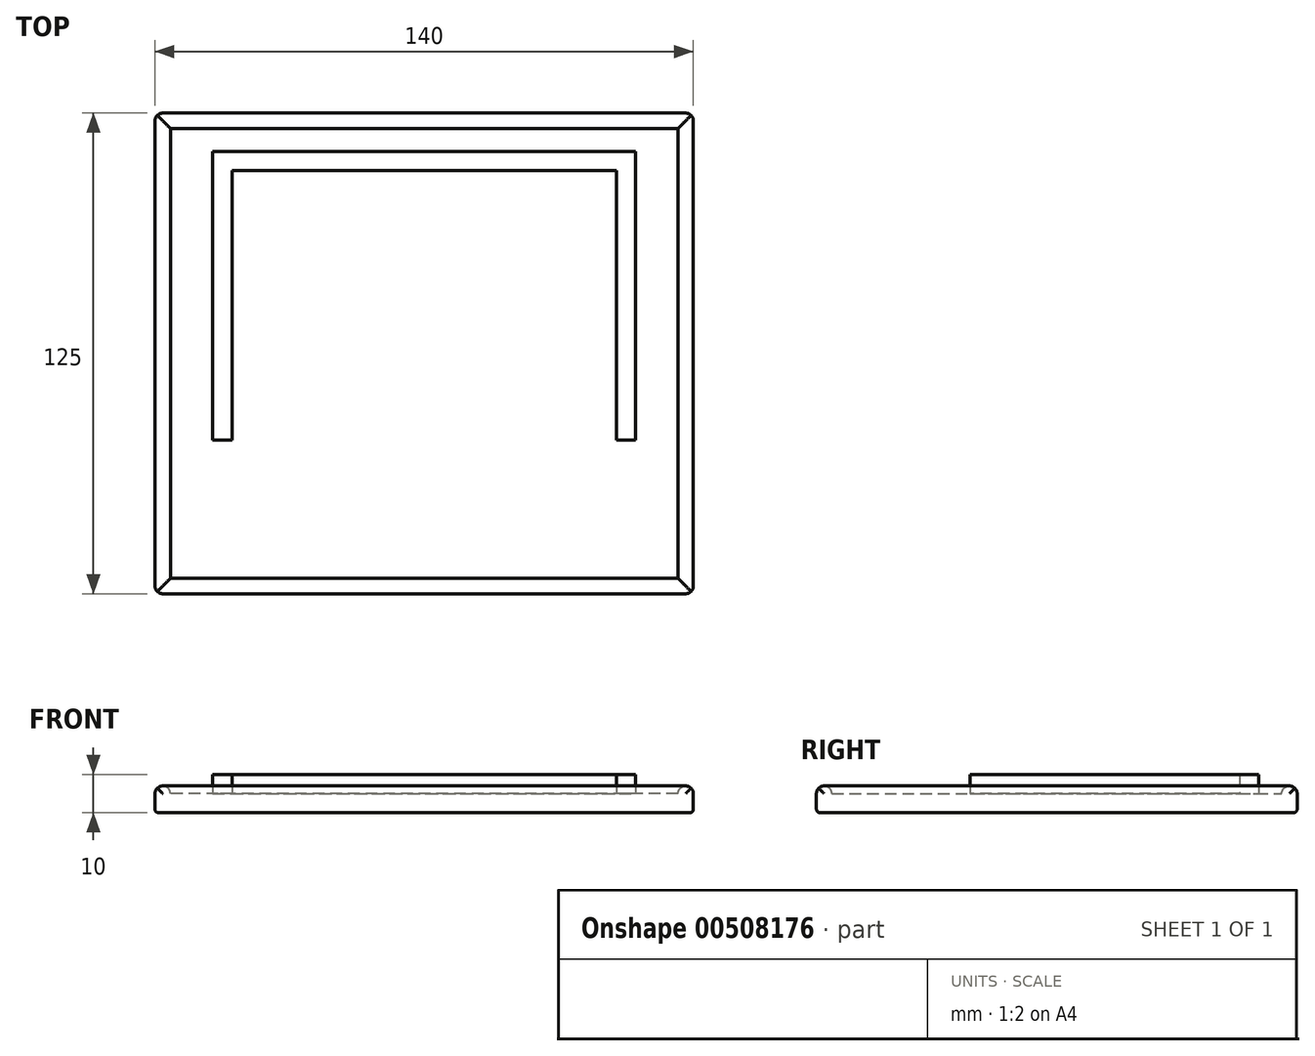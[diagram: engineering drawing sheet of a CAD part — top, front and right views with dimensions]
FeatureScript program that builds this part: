
annotation { "Feature Type Name" : "Feature", "Feature Type Description" : "" }
export const myFeature = defineFeature(function(context is Context, id is Id, definition is map)
    precondition{}
    {
        {
            var Q0;
            Q0=qCreatedBy(makeId("Top.planeOp"),FACE);
            var sketch = newSketch(context, id + "F0", { "sketchPlane" : qUnion([Q0])});
            skLineSegment(sketch, "E0.bottom", {"start": v(70, 62.5) * mm, "end": v(-70, 62.5) * mm});
            skLineSegment(sketch, "E0.top", {"start": v(70, -62.5) * mm, "end": v(-70, -62.5) * mm});
            skLineSegment(sketch, "E0.left", {"start": v(70, 62.5) * mm, "end": v(70, -62.5) * mm});
            skLineSegment(sketch, "E0.right", {"start": v(-70, 62.5) * mm, "end": v(-70, -62.5) * mm});
            skPoint(sketch, "E0.middle", {"position": v(0, 0) * mm});
            skSolve(sketch);
        }
        {
            var Q0;
            Q0=makeQuery(id+"F0.imprint","IMPRINT",FACE,{"disambiguationData":[TD([[makeQuery(id+"F0.imprint","IMPRINT",EDGE,{"derivedFrom":sQuery(id+"F0.wireOp",EDGE,"E0.bottom")}),1.0]])]});
            extrude(context, id + "F1", {"entities" : qUnion([Q0]), "depth" : 5 * mm, "offsetDistance" : 25 * mm});
        }
        {
            var Q0;
            Q0=makeQuery(id+"F1.opExtrude","CAP_FACE",FACE,{"disambiguationData":[OSD([sQuery(id+"F0.wireOp",EDGE,"E0.bottom"),sQuery(id+"F0.wireOp",EDGE,"E0.top"),sQuery(id+"F0.wireOp",EDGE,"E0.left"),sQuery(id+"F0.wireOp",EDGE,"E0.right")])],"isStart":false});
            var sketch = newSketch(context, id + "F2", { "sketchPlane" : qUnion([Q0])});
            skLineSegment(sketch, "E1", {"start": v(23.4, -62.5) * mm, "end": v(23.4, -22.5) * mm});
            skLineSegment(sketch, "E2", {"start": v(55, -22.5) * mm, "end": v(-55, -22.5) * mm});
            skLineSegment(sketch, "E3", {"start": v(-55, -22.5) * mm, "end": v(-55, 52.5) * mm});
            skLineSegment(sketch, "E4", {"start": v(-55, 52.5) * mm, "end": v(55, 52.5) * mm});
            skLineSegment(sketch, "E5", {"start": v(55, 52.5) * mm, "end": v(55, -22.5) * mm});
            skLineSegment(sketch, "E6", {"start": v(-50, 47.5) * mm, "end": v(50, 47.5) * mm});
            skLineSegment(sketch, "E7", {"start": v(50, 47.5) * mm, "end": v(50, -17.5) * mm});
            skLineSegment(sketch, "E8", {"start": v(-50, 47.5) * mm, "end": v(-50, -17.5) * mm});
            skLineSegment(sketch, "E9", {"start": v(-50, -17.5) * mm, "end": v(50, -17.5) * mm});
            skLineSegment(sketch, "E10", {"start": v(-66, 58.5) * mm, "end": v(66, 58.5) * mm});
            skLineSegment(sketch, "E11", {"start": v(66, 58.5) * mm, "end": v(66, -58.5) * mm});
            skLineSegment(sketch, "E12", {"start": v(66, -58.5) * mm, "end": v(-66, -58.5) * mm});
            skLineSegment(sketch, "E13", {"start": v(-66, -58.5) * mm, "end": v(-66, 58.5) * mm});
            skLineSegment(sketch, "E14", {"start": v(-50, -17.5) * mm, "end": v(-50, -22.5) * mm});
            skLineSegment(sketch, "E15", {"start": v(50, -17.5) * mm, "end": v(50, -22.5) * mm});
            skSolve(sketch);
        }
        {
            var Q0;
            {var subQ0=sQuery(id+"F2.wireOp",EDGE,"E3");Q0=makeQuery(id+"F2.imprint","IMPRINT",FACE,{"disambiguationData":[TD([[makeQuery(id+"F2.imprint","IMPRINT",EDGE,{"derivedFrom":subQ0}),-1.0]])]});}
            extrude(context, id + "F3", {"entities" : qUnion([Q0]), "operationType" : NewBodyOperationType.ADD, "depth" : 5 * mm, "offsetDistance" : 25 * mm});
        }
        {
            var Q0;
            Q0=makeQuery(id+"F2.imprint","IMPRINT",FACE,{"disambiguationData":[TD([[makeQuery(id+"F2.imprint","IMPRINT",EDGE,{"derivedFrom":sQuery(id+"F2.wireOp",EDGE,"E10")}),1.0]])]});
            extrude(context, id + "F4", {"entities" : qUnion([Q0]), "operationType" : NewBodyOperationType.ADD, "depth" : 2 * mm, "offsetDistance" : 25 * mm});
        }
        {
            var Q0;
            Q0=makeQuery(id+"F4.opExtrude","CAP_EDGE",EDGE,{"disambiguationData":[OSD([sQuery(id+"F2.wireOp",EDGE,"E13")])],"isStart":false});
            var Q1;
            Q1=makeQuery(id+"F4.opExtrude","CAP_EDGE",EDGE,{"disambiguationData":[OSD([sQuery(id+"F0.wireOp",EDGE,"E0.right")])],"isStart":false});
            var Q2;
            Q2=makeQuery(id+"F4.opExtrude","CAP_EDGE",EDGE,{"disambiguationData":[OSD([sQuery(id+"F2.wireOp",EDGE,"E10")])],"isStart":false});
            var Q3;
            Q3=makeQuery(id+"F4.opExtrude","CAP_EDGE",EDGE,{"disambiguationData":[OSD([sQuery(id+"F0.wireOp",EDGE,"E0.bottom")])],"isStart":false});
            var Q4;
            Q4=makeQuery(id+"F4.opExtrude","CAP_EDGE",EDGE,{"disambiguationData":[OSD([sQuery(id+"F2.wireOp",EDGE,"E12")])],"isStart":false});
            var Q5;
            Q5=makeQuery(id+"F4.opExtrude","CAP_EDGE",EDGE,{"disambiguationData":[OSD([sQuery(id+"F0.wireOp",EDGE,"E0.top")])],"isStart":false});
            var Q6;
            Q6=makeQuery(id+"F4.opExtrude","CAP_EDGE",EDGE,{"disambiguationData":[OSD([sQuery(id+"F2.wireOp",EDGE,"E11")])],"isStart":false});
            var Q7;
            Q7=makeQuery(id+"F4.opExtrude","CAP_EDGE",EDGE,{"disambiguationData":[OSD([sQuery(id+"F0.wireOp",EDGE,"E0.left")])],"isStart":false});
            fillet(context, id + "F5", {"entities" : qUnion([Q0, Q1, Q2, Q3, Q4, Q5, Q6, Q7]), "radius" : 2 * mm, "tangentPropagation" : true, "allowEdgeOverflow" : false});
        }
        {
            var Q0;
            {var subQ0=sQuery(id+"F0.wireOp",EDGE,"E0.right");var subQ1=sQuery(id+"F0.wireOp",EDGE,"E0.bottom");Q0=makeQuery(id+"F4.boolean.opBoolean","MERGE",EDGE,{"derivedFrom":[makeQuery(id+"F1.opExtrude","SWEPT_EDGE",EDGE,{"disambiguationData":[OSD([subQ1,subQ0])]}),makeQuery(id+"F4.opExtrude","SWEPT_EDGE",EDGE,{"disambiguationData":[OSD([subQ1,subQ0])]})]});}
            var Q1;
            {var subQ0=sQuery(id+"F0.wireOp",EDGE,"E0.right");var subQ1=sQuery(id+"F0.wireOp",EDGE,"E0.top");Q1=makeQuery(id+"F4.boolean.opBoolean","MERGE",EDGE,{"derivedFrom":[makeQuery(id+"F1.opExtrude","SWEPT_EDGE",EDGE,{"disambiguationData":[OSD([subQ1,subQ0])]}),makeQuery(id+"F4.opExtrude","SWEPT_EDGE",EDGE,{"disambiguationData":[OSD([subQ1,subQ0])]})]});}
            var Q2;
            {var subQ0=sQuery(id+"F0.wireOp",EDGE,"E0.left");var subQ1=sQuery(id+"F0.wireOp",EDGE,"E0.top");Q2=makeQuery(id+"F4.boolean.opBoolean","MERGE",EDGE,{"derivedFrom":[makeQuery(id+"F1.opExtrude","SWEPT_EDGE",EDGE,{"disambiguationData":[OSD([subQ1,subQ0])]}),makeQuery(id+"F4.opExtrude","SWEPT_EDGE",EDGE,{"disambiguationData":[OSD([subQ1,subQ0])]})]});}
            var Q3;
            {var subQ0=sQuery(id+"F0.wireOp",EDGE,"E0.left");var subQ1=sQuery(id+"F0.wireOp",EDGE,"E0.bottom");Q3=makeQuery(id+"F4.boolean.opBoolean","MERGE",EDGE,{"derivedFrom":[makeQuery(id+"F1.opExtrude","SWEPT_EDGE",EDGE,{"disambiguationData":[OSD([subQ1,subQ0])]}),makeQuery(id+"F4.opExtrude","SWEPT_EDGE",EDGE,{"disambiguationData":[OSD([subQ1,subQ0])]})]});}
            fillet(context, id + "F6", {"entities" : qUnion([Q0, Q1, Q2, Q3]), "radius" : 2 * mm, "tangentPropagation" : true, "allowEdgeOverflow" : false});
        }
        {
            var Q0;
            Q0=makeQuery(id+"F1.opExtrude","CAP_EDGE",EDGE,{"disambiguationData":[OSD([sQuery(id+"F0.wireOp",EDGE,"E0.top")])],"isStart":true});
            var Q1;
            Q1=makeQuery(id+"F1.opExtrude","CAP_EDGE",EDGE,{"disambiguationData":[OSD([sQuery(id+"F0.wireOp",EDGE,"E0.right")])],"isStart":true});
            var Q2;
            {var subQ0=sQuery(id+"F0.wireOp",EDGE,"E0.right");var subQ1=sQuery(id+"F0.wireOp",EDGE,"E0.top");Q2=makeQuery(id+"F6.opFillet","BLEND_EDGE",EDGE,{"blendedFrom":[makeQuery(id+"F4.boolean.opBoolean","MERGE",EDGE,{"derivedFrom":[makeQuery(id+"F1.opExtrude","SWEPT_EDGE",EDGE,{"disambiguationData":[OSD([subQ1,subQ0])]}),makeQuery(id+"F4.opExtrude","SWEPT_EDGE",EDGE,{"disambiguationData":[OSD([subQ1,subQ0])]})]}),makeQuery(id+"F1.opExtrude","CAP_FACE",FACE,{"disambiguationData":[OSD([sQuery(id+"F0.wireOp",EDGE,"E0.bottom"),subQ1,sQuery(id+"F0.wireOp",EDGE,"E0.left"),subQ0])],"isStart":true})],"blendedInto":[makeQuery(id+"F1.opExtrude","CAP_FACE",FACE,{"disambiguationData":[OSD([sQuery(id+"F0.wireOp",EDGE,"E0.bottom"),subQ1,sQuery(id+"F0.wireOp",EDGE,"E0.left"),subQ0])],"isStart":true})]});}
            var Q3;
            {var subQ0=sQuery(id+"F0.wireOp",EDGE,"E0.right");var subQ1=sQuery(id+"F0.wireOp",EDGE,"E0.bottom");Q3=makeQuery(id+"F6.opFillet","BLEND_EDGE",EDGE,{"blendedFrom":[makeQuery(id+"F4.boolean.opBoolean","MERGE",EDGE,{"derivedFrom":[makeQuery(id+"F1.opExtrude","SWEPT_EDGE",EDGE,{"disambiguationData":[OSD([subQ1,subQ0])]}),makeQuery(id+"F4.opExtrude","SWEPT_EDGE",EDGE,{"disambiguationData":[OSD([subQ1,subQ0])]})]}),makeQuery(id+"F1.opExtrude","CAP_FACE",FACE,{"disambiguationData":[OSD([subQ1,sQuery(id+"F0.wireOp",EDGE,"E0.top"),sQuery(id+"F0.wireOp",EDGE,"E0.left"),subQ0])],"isStart":true})],"blendedInto":[makeQuery(id+"F1.opExtrude","CAP_FACE",FACE,{"disambiguationData":[OSD([subQ1,sQuery(id+"F0.wireOp",EDGE,"E0.top"),sQuery(id+"F0.wireOp",EDGE,"E0.left"),subQ0])],"isStart":true})]});}
            var Q4;
            Q4=makeQuery(id+"F1.opExtrude","CAP_EDGE",EDGE,{"disambiguationData":[OSD([sQuery(id+"F0.wireOp",EDGE,"E0.bottom")])],"isStart":true});
            var Q5;
            {var subQ0=sQuery(id+"F0.wireOp",EDGE,"E0.left");var subQ1=sQuery(id+"F0.wireOp",EDGE,"E0.top");Q5=makeQuery(id+"F6.opFillet","BLEND_EDGE",EDGE,{"blendedFrom":[makeQuery(id+"F4.boolean.opBoolean","MERGE",EDGE,{"derivedFrom":[makeQuery(id+"F1.opExtrude","SWEPT_EDGE",EDGE,{"disambiguationData":[OSD([subQ1,subQ0])]}),makeQuery(id+"F4.opExtrude","SWEPT_EDGE",EDGE,{"disambiguationData":[OSD([subQ1,subQ0])]})]}),makeQuery(id+"F1.opExtrude","CAP_FACE",FACE,{"disambiguationData":[OSD([sQuery(id+"F0.wireOp",EDGE,"E0.bottom"),subQ1,subQ0,sQuery(id+"F0.wireOp",EDGE,"E0.right")])],"isStart":true})],"blendedInto":[makeQuery(id+"F1.opExtrude","CAP_FACE",FACE,{"disambiguationData":[OSD([sQuery(id+"F0.wireOp",EDGE,"E0.bottom"),subQ1,subQ0,sQuery(id+"F0.wireOp",EDGE,"E0.right")])],"isStart":true})]});}
            var Q6;
            Q6=makeQuery(id+"F1.opExtrude","CAP_EDGE",EDGE,{"disambiguationData":[OSD([sQuery(id+"F0.wireOp",EDGE,"E0.left")])],"isStart":true});
            var Q7;
            {var subQ0=sQuery(id+"F0.wireOp",EDGE,"E0.left");var subQ1=sQuery(id+"F0.wireOp",EDGE,"E0.bottom");Q7=makeQuery(id+"F6.opFillet","BLEND_EDGE",EDGE,{"blendedFrom":[makeQuery(id+"F4.boolean.opBoolean","MERGE",EDGE,{"derivedFrom":[makeQuery(id+"F1.opExtrude","SWEPT_EDGE",EDGE,{"disambiguationData":[OSD([subQ1,subQ0])]}),makeQuery(id+"F4.opExtrude","SWEPT_EDGE",EDGE,{"disambiguationData":[OSD([subQ1,subQ0])]})]}),makeQuery(id+"F1.opExtrude","CAP_FACE",FACE,{"disambiguationData":[OSD([subQ1,sQuery(id+"F0.wireOp",EDGE,"E0.top"),subQ0,sQuery(id+"F0.wireOp",EDGE,"E0.right")])],"isStart":true})],"blendedInto":[makeQuery(id+"F1.opExtrude","CAP_FACE",FACE,{"disambiguationData":[OSD([subQ1,sQuery(id+"F0.wireOp",EDGE,"E0.top"),subQ0,sQuery(id+"F0.wireOp",EDGE,"E0.right")])],"isStart":true})]});}
            fillet(context, id + "F7", {"entities" : qUnion([Q0, Q1, Q2, Q3, Q4, Q5, Q6, Q7]), "radius" : 1 * mm, "tangentPropagation" : true, "allowEdgeOverflow" : false});
        }
    });
